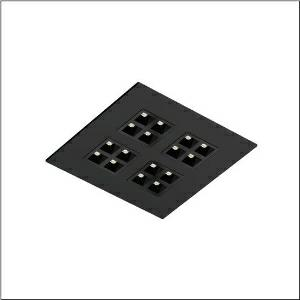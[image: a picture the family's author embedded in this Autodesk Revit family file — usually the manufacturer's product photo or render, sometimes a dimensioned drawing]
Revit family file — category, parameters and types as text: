
# Revit family: silica_r__31_square_51my6ldu34ba_0a8f
name_source: partatom
category: Lighting Fixtures
units: mm (PartAtom-declared; Revit-internal decimal feet)

## family parameters
Cut with Voids When Loaded = No
Host = Face
Light Source = No
Part Type = Normal
Room Calculation Point = No
Round Connector Dimension = Use Diameter
Shared = No

## types (1)
- --- (1 x LED, 5980 lm, 38.5 W, 3000K)
    Apparent Load = 39 VA
    CIE Flux Codes = 82 100 100 100 100
    Color Rendering = 80
    Color Temperature = 3000K
    Default Elevation = 1800 mm
    Description = Silica® 31 Square, office luminaire, primary light control with lens, of PMMA, primary anti-glare with reflector, of PC, black, light emission: direct distribution, primary light characteristic: symmetric, installation type: lay-in mounting, LED, rated luminous flux: 4.650lm, luminous efficacy: 158lm/W, light colour: 830, colour temperature: 3000K, control gear: DALI 2, Multilumen, with terminal, 5-pole, mains connection: 220..240V, AC, 50/60Hz, rated input power: 29.4W, luminaire housing, of sheet steel, coated, jet black (RAL 9005), module: M625, length: 620mm, width: 620mm, height: 43mm, protection rating (complete): IP20, insulation class (complete): insulation class II (safety insulation), certification: CE, impact resistance: IK03, permissible operating ambient temperature: -20..+35°C, standard: EN 50419, packaging unit: 1 piece
    Height = 0 mm  [stored 0 ft]
    Lamp = 1 x LED
    Lamp Light Flux = 5980 lm
    Lamp Power = 38.5 W
    Lamp count = 1
    Length = 620 mm
    Luminous efficacy = 155 lm/W
    Manufacturer = Siteco
    ModVariant = No
    Model = 51MY6LDU34BA
    Mounting Place = Ceiling
    Mounting Type = Recessed
    Number of Poles = 1
    OnlyDefault = Yes
    Power Factor = 1
    Product Name = Silica® 31 Square
    Product group = office luminaire | ceiling recessed
    ProductGroupID = 401
    Protection Class = Protection class II
    Protection Degree = IP 20
    RLX_Detail_Level = 1
    RLX_Emergency_Light_Flux = 0 lm
    RLX_Emergency_Type = 0
    RLX_Emergency_Type_DB = No
    RlxData = <blob elided: 35513 chars, md5=bd227b2b>
    Socket = socket
    Standby Power = 0 W
    System Light Flux = 5980 lm
    System Power = 39 W
    Type Comments = factory setting: luminous flux: 100 % | (OFF | OFF | OFF | OFF) | 1050 mA
    Type Image = l_1313660.jpg
    URL = http://relux.com
    VarID = @adj_036230
    Voltage = 0 V
    Weight = 0.00 kg
    Width = 620 mm

note: [stored X ft] marks values corroborated as IEEE doubles in the binary element streams (Revit-internal decimal feet)

## geometry (parser evidence)
native form markers: Blend x4, Sweep x11
no freeform markers — native parametric forms only
